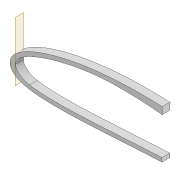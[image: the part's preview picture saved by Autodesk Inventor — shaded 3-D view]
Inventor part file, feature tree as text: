
AUTODESK INVENTOR PART (.ipt)
format: ipt  version: 2022 (Build 260153000, 153)  size: 488,448 bytes
history: native  units: mm
features: sketch x5, extrude x4, thicken_offset x3, projected_geometry x2, shell x1, plane x1, other x1, fillet x1
ambient origin geometry x8: Origin, YZ Plane, XZ Plane, XY Plane, X Axis, Y Axis, Z Axis, Center Point
bodies: Solid1 (feature_tree)
feature tree (18):
  extrude  "Extrusion1"  Depth=3.0mm
  shell  "Shell1"  Thickness=1.0mm
  thicken_offset  "Thicken1"
  extrude  "Extrusion27"  TaperAngle=0.0deg  [1 undecoded]
  thicken_offset  "Thicken3"
  extrude  "Extrusion29"  Depth=20.0mm
  plane  "Work Plane5"
  other  "Bend Part2"
  thicken_offset  "Thicken5"
  extrude  "Extrusion30"  Depth=10.0mm TaperAngle=0.0deg
  fillet  "Fillet6"  Radius=10.0mm
  sketch  "Sketch3"  dims[d0=10.0mm d1=0.0mm d2=3.0mm d159=1.0mm d160=2.0mm]
  sketch  "Sketch48"  dims[d236=190.0mm d237=0.0mm d238=0.0mm]
  sketch  "Sketch55"  dims[d249=2.0mm d250=1.0mm d254=20.0mm]
  projected_geometry  "Projected Loop32"
  sketch  "Sketch57"  dims[d255=8.0mm d256=10.0mm d257=0.0mm d262=10.0mm d263=0.174533mm]
  sketch  "Sketch58"  dims[d264=1.0mm d265=1.0mm d268=80.0mm d269=4.0mm d270=10.0mm d271=0.0mm d272=500.0mm d273=300.0mm]
  projected_geometry  "Projected Loop34"
note: 1 required parameter value undecoded (feature->parameter linkage not recoverable at this tier; creation-order binding heuristic only, values carry confidence <= 0.55)
